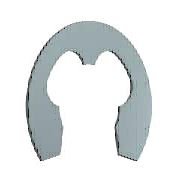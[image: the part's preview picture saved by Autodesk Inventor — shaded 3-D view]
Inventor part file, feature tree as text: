
AUTODESK INVENTOR PART (.ipt)
format: ipt  version: 2023.1 (Build 271208000, 208)  size: 157,184 bytes
history: native  units: mm (DEFAULTED — no unit token found)
features: other x2, plane x1
ambient origin geometry x8: Origin, YZ Plane, XZ Plane, XY Plane, X Axis, Y Axis, Z Axis, Center Point
bodies: Solid1 (feature_tree), Body (feature_tree)
feature tree (3):
  other  "Work Axis1"
  other  "Work Axis2"
  plane  "Work Plane1"
